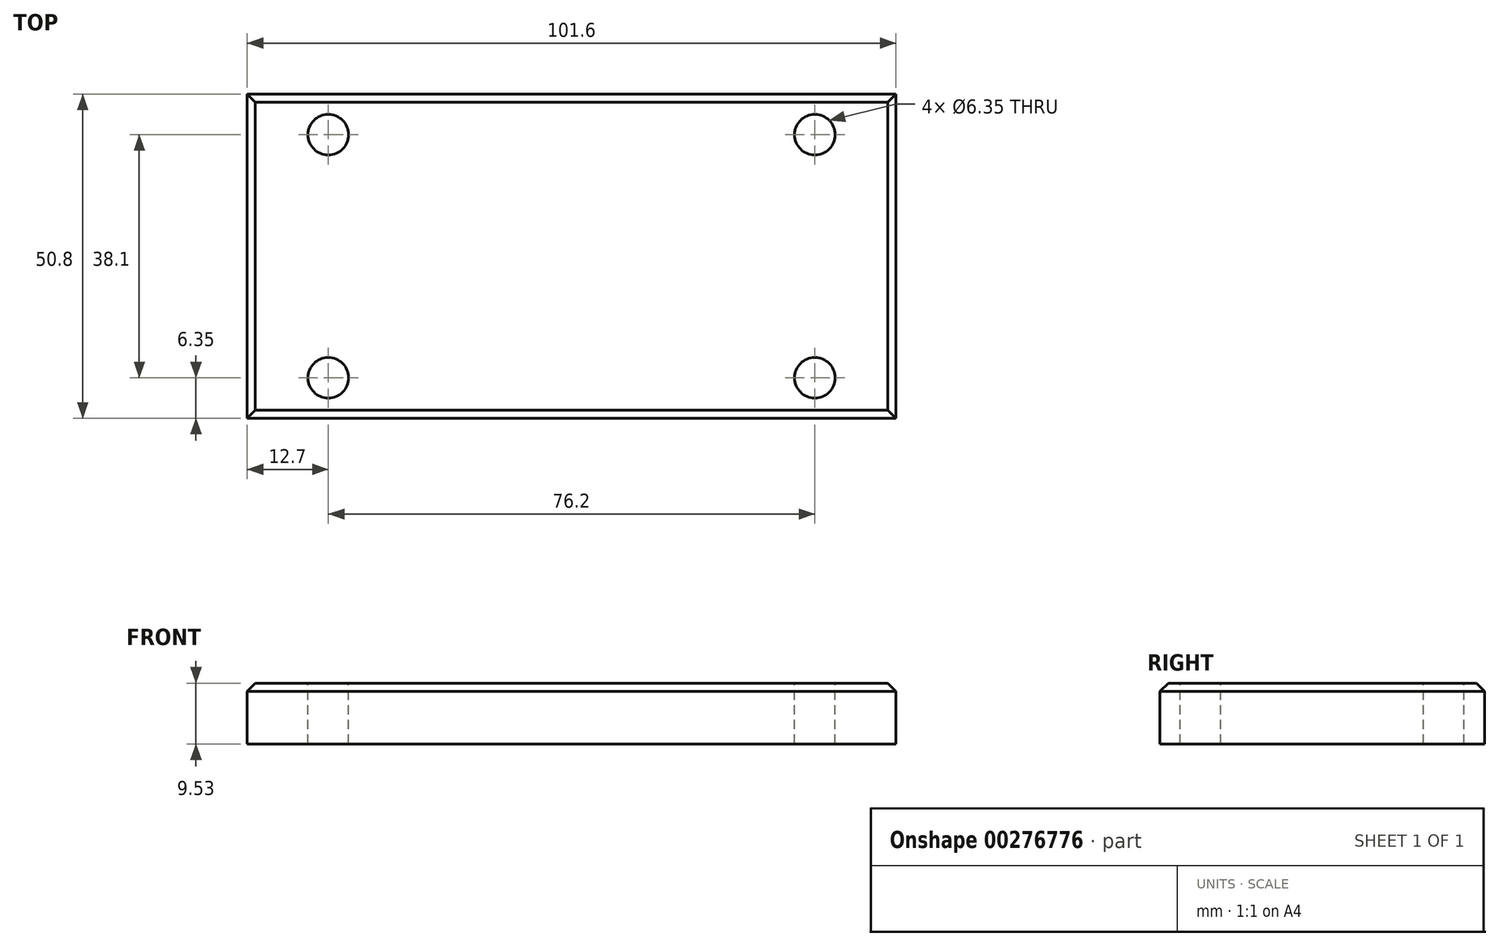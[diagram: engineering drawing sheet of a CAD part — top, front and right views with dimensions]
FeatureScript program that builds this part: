
annotation { "Feature Type Name" : "Feature", "Feature Type Description" : "" }
export const myFeature = defineFeature(function(context is Context, id is Id, definition is map)
    precondition{}
    {
        {
            var Q0;
            Q0=qCreatedBy(makeId("Top.planeOp"),FACE);
            var sketch = newSketch(context, id + "F0", { "sketchPlane" : qUnion([Q0])});
            skLineSegment(sketch, "E0.bottom", {"start": v(50.8, -25.4) * mm, "end": v(-50.8, -25.4) * mm});
            skLineSegment(sketch, "E0.top", {"start": v(50.8, 25.4) * mm, "end": v(-50.8, 25.4) * mm});
            skLineSegment(sketch, "E0.left", {"start": v(50.8, -25.4) * mm, "end": v(50.8, 25.4) * mm});
            skLineSegment(sketch, "E0.right", {"start": v(-50.8, -25.4) * mm, "end": v(-50.8, 25.4) * mm});
            skPoint(sketch, "E0.middle", {"position": v(0, 0) * mm});
            skLineSegment(sketch, "E1", {"start": v(-50.8, 0) * mm, "end": v(50.8, 0) * mm, "construction": true});
            skLineSegment(sketch, "E2", {"start": v(0, 25.4) * mm, "end": v(0, -25.4) * mm, "construction": true});
            skCircle(sketch, "E3", {"center": v(-38.1, 19.05) * mm, "radius": 3.18 * mm});
            skCircle(sketch, "E4", {"center": v(38.1, 19.05) * mm, "radius": 3.18 * mm});
            skCircle(sketch, "E5", {"center": v(38.1, -19.05) * mm, "radius": 3.18 * mm});
            skCircle(sketch, "E6", {"center": v(-38.1, -19.05) * mm, "radius": 3.18 * mm});
            skSolve(sketch);
        }
        {
            var Q0;
            Q0 = qSketchRegion(id + "F0", true);
            extrude(context, id + "F1", {"entities" : qUnion([Q0]), "oppositeDirection" : true, "depth" : 9.52 * mm});
        }
        {
            var Q0;
            Q0=makeQuery(id+"F1.opExtrude","CAP_EDGE",EDGE,{"disambiguationData":[OSD([sQuery(id+"F0.wireOp",EDGE,"E0.right")])],"isStart":true});
            var Q1;
            Q1=makeQuery(id+"F1.opExtrude","CAP_EDGE",EDGE,{"disambiguationData":[OSD([sQuery(id+"F0.wireOp",EDGE,"E0.bottom")])],"isStart":true});
            var Q2;
            Q2=makeQuery(id+"F1.opExtrude","CAP_EDGE",EDGE,{"disambiguationData":[OSD([sQuery(id+"F0.wireOp",EDGE,"E0.top")])],"isStart":true});
            var Q3;
            Q3=makeQuery(id+"F1.opExtrude","CAP_EDGE",EDGE,{"disambiguationData":[OSD([sQuery(id+"F0.wireOp",EDGE,"E0.left")])],"isStart":true});
            chamfer(context, id + "F2", {"entities" : qUnion([Q0, Q1, Q2, Q3]), "chamferType" : ChamferType.OFFSET_ANGLE, "width" : 1.27 * mm, "oppositeDirection" : false, "angle" : 45 * degree, "tangentPropagation" : true});
        }
    });
